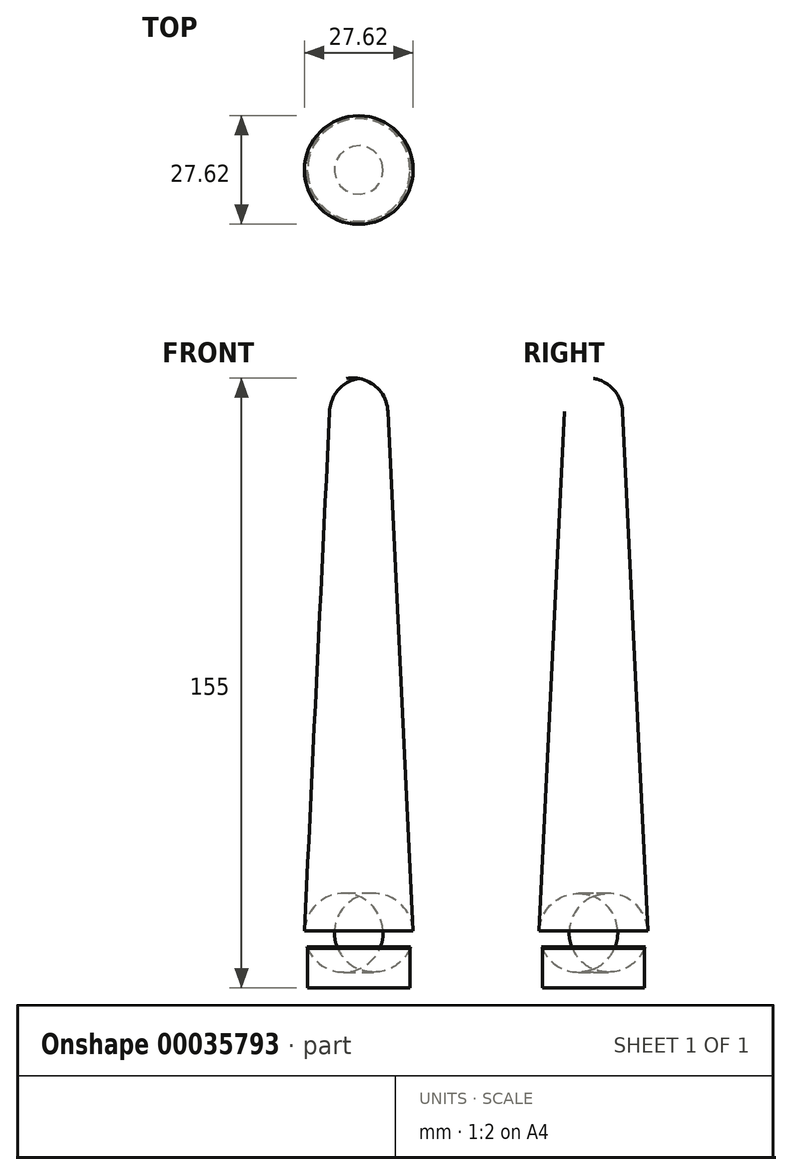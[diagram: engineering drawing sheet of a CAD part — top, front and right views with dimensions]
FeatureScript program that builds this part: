
annotation { "Feature Type Name" : "Feature", "Feature Type Description" : "" }
export const myFeature = defineFeature(function(context is Context, id is Id, definition is map)
    precondition{}
    {
        {
            var Q0;
            Q0=qCreatedBy(makeId("Front.planeOp"),FACE);
            var sketch = newSketch(context, id + "F0", { "sketchPlane" : qUnion([Q0])});
            skLineSegment(sketch, "E0", {"start": v(-13, 0) * mm, "end": v(0, 0) * mm});
            skLineSegment(sketch, "E1", {"start": v(0, 0) * mm, "end": v(0, 145) * mm});
            skPoint(sketch, "E2", {"position": v(0, 72.5) * mm});
            skLineSegment(sketch, "E3.top", {"start": v(-13, -10) * mm, "end": v(0, -10) * mm});
            skLineSegment(sketch, "E3.left", {"start": v(-13, 0) * mm, "end": v(-13, -10) * mm});
            skLineSegment(sketch, "E3.right", {"start": v(0, 0) * mm, "end": v(0, -10) * mm});
            skPoint(sketch, "E4.visualSharp", {"position": v(-13, 0) * mm});
            skLineSegment(sketch, "E5", {"start": v(-13, 0) * mm, "end": v(-13.18, 0.47) * mm});
            skLineSegment(sketch, "E6", {"start": v(-13.8, 4.48) * mm, "end": v(-7.41, 136.44) * mm});
            skLineSegment(sketch, "E7", {"start": v(0, 145) * mm, "end": v(1.57, 145) * mm});
            skPoint(sketch, "E8.visualSharp", {"position": v(-7, 145) * mm});
            skArc(sketch, "E8.filletArc", {"start": v(1.57, 145) * mm, "mid": v(-4.63, 142.52) * mm, "end": v(-7.41, 136.44) * mm});
            skPoint(sketch, "E9.visualSharp", {"position": v(-13.9, 2.4) * mm});
            skArc(sketch, "E9.filletArc", {"start": v(-13.8, 4.48) * mm, "mid": v(-13.7, 2.44) * mm, "end": v(-13.18, 0.47) * mm});
            skSolve(sketch);
        }
        {
            var Q0;
            {var subQ4=sQuery(id+"F0.wireOp",EDGE,"E0");Q0=makeQuery(id+"F0.imprint","IMPRINT",FACE,{"disambiguationData":[TD([[makeQuery(id+"F0.imprint","IMPRINT",EDGE,{"derivedFrom":subQ4}),1.0]])]});}
            var Q1;
            Q1=makeQuery(id+"F0.imprint","IMPRINT",FACE,{"disambiguationData":[TD([[makeQuery(id+"F0.imprint","IMPRINT",EDGE,{"derivedFrom":sQuery(id+"F0.wireOp",EDGE,"E0")}),-1.0]])]});
            var Q2;
            Q2=sQuery(id+"F0.wireOp",EDGE,"E1");
            revolve(context, id + "F1", {"entities" : qUnion([Q0, Q1]), "axis" : qUnion([Q2]), "revolveType" : RevolveType.FULL});
        }
    });
